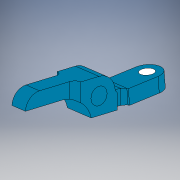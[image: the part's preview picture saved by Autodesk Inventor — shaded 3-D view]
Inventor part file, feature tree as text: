
AUTODESK INVENTOR PART (.ipt)
format: ipt  version: 2018 (Build 220112000, 112)  size: 208,384 bytes
history: native  units: mm
features: sketch x4, extrude x3, projected_geometry x3, other x2, thread x1, fillet x1, direct_edit x1
ambient origin geometry x8: Origin, YZ Plane, XZ Plane, XY Plane, X Axis, Y Axis, Z Axis, Center Point
bodies: Solid1 (feature_tree)
feature tree (15):
  extrude  "Extrusion1"  Depth=4.7mm
  extrude  "Extrusion2"  Depth=4.0mm
  extrude  "Extrusion3"  Depth=1.3mm
  thread  "Thread1"  [1 undecoded]
  other  "Bend Part1"
  fillet  "Fillet1"  Radius=3.5mm
  direct_edit  "Direct Edit1"
  sketch  "Sketch1"  dims[d0=8.0mm d1=4.7mm]
  sketch  "Sketch2"  dims[d2=3.5mm d4=4.0mm]
  sketch  "Sketch3"  dims[d5=12.0mm d7=1.3mm d8=4.0mm d9=3.5mm]
  sketch  "Sketch4"  dims[d10=9.18mm d11=16.98mm d12=14.0mm d13=0.0mm d14=4.0mm d15=31.85mm d16=7.0mm d17=3.02mm d18=22.98mm d19=1.5mm d20=10.98mm d21=14.0mm d22=0.0mm d23=3.24mm d24=14.0mm d25=0.0mm d26=10.0mm d27=0.0mm d28=23.5mm d29=10.0mm d30=0.872665mm d31=1.0mm d32=6.5mm]
  projected_geometry  "Project Cut Edges1"
  projected_geometry  "Project Cut Edges2"
  projected_geometry  "Project Cut Edges3"
  other  "Size1"
note: 1 required parameter value undecoded (feature->parameter linkage not recoverable at this tier; creation-order binding heuristic only, values carry confidence <= 0.55)
